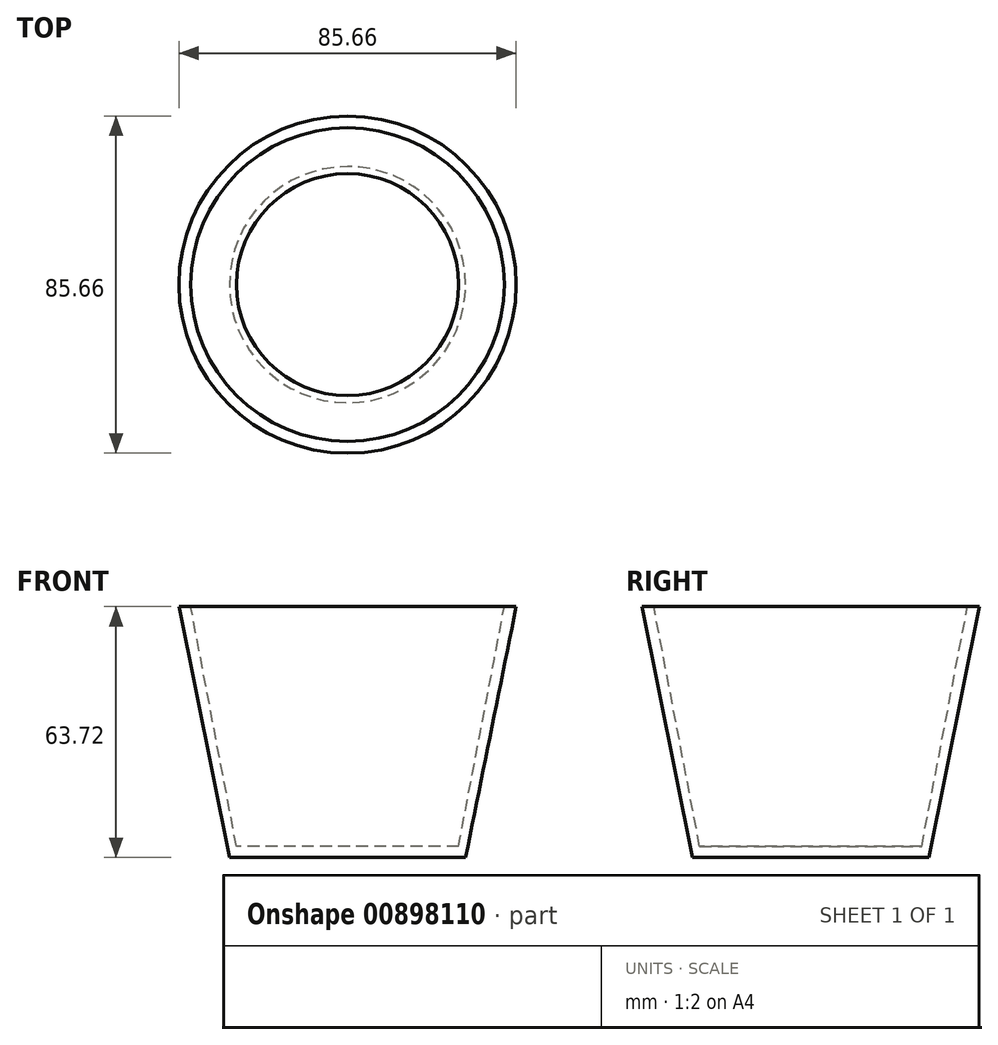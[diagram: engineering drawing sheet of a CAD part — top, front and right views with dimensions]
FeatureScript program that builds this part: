
annotation { "Feature Type Name" : "Feature", "Feature Type Description" : "" }
export const myFeature = defineFeature(function(context is Context, id is Id, definition is map)
    precondition{}
    {
        {
            var Q0;
            Q0=qCreatedBy(makeId("Front.planeOp"),FACE);
            var sketch = newSketch(context, id + "F0", { "sketchPlane" : qUnion([Q0])});
            skLineSegment(sketch, "E0", {"start": v(0, 78.28) * mm, "end": v(0, -61.74) * mm});
            skLineSegment(sketch, "E1", {"start": v(0, 0) * mm, "end": v(-30, 0) * mm});
            skLineSegment(sketch, "E2", {"start": v(-30, 0) * mm, "end": v(-42.83, 63.72) * mm});
            skLineSegment(sketch, "E3", {"start": v(-42.83, 63.72) * mm, "end": v(-39.83, 63.72) * mm});
            skLineSegment(sketch, "E4", {"start": v(-39.83, 63.72) * mm, "end": v(-28.2, 2.82) * mm});
            skLineSegment(sketch, "E5", {"start": v(-28.2, 2.82) * mm, "end": v(0, 2.82) * mm});
            skLineSegment(sketch, "E6", {"start": v(0, 2.82) * mm, "end": v(0, 0) * mm});
            skSolve(sketch);
        }
        {
            var Q0;
            {var subQ0=sQuery(id+"F0.wireOp",EDGE,"E1");Q0=makeQuery(id+"F0.imprint","IMPRINT",FACE,{"disambiguationData":[TD([[makeQuery(id+"F0.imprint","IMPRINT",EDGE,{"derivedFrom":subQ0}),-1.0]])]});}
            var Q1;
            Q1=sQuery(id+"F0.wireOp",EDGE,"E0");
            revolve(context, id + "F1", {"surfaceOperationType" : NewSurfaceOperationType.NEW, "entities" : qUnion([Q0]), "axis" : qUnion([Q1]), "revolveType" : RevolveType.FULL});
        }
    });
